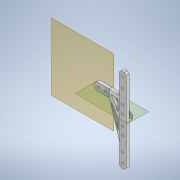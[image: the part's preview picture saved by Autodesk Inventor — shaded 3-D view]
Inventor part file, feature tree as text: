
AUTODESK INVENTOR PART (.ipt)
format: ipt  version: 2023 (Build 270158000, 158)  size: 307,200 bytes
history: native  units: mm
features: other x8, projected_geometry x7, sketch x6, extrude x5, fillet x4, plane x3, reference x3, chamfer x2, loft x1
ambient origin geometry x8: Origin, YZ Plane, XZ Plane, XY Plane, X Axis, Y Axis, Z Axis, Center Point
bodies: Solid1 (feature_tree)
feature tree (39):
  extrude  "Extrusion1"  Depth=87.0mm
  plane  "Work Plane1"
  plane  "Work Plane2"
  extrude  "Extrusion2"  Depth=2.0mm
  sketch  "Sketch3"  dims[d4=2.0mm d5=2.0mm]
  loft  "Loft1"
  plane  "Work Plane3"
  extrude  "Extrusion3"  Depth=8.0mm
  fillet  "Fillet1"  Radius=15.0mm
  extrude  "Extrusion4"  Depth=2.0mm
  fillet  "Fillet2"  Radius=3.0mm
  fillet  "Fillet3"  Radius=3.0mm
  chamfer  "Chamfer1"  Distance=3.0mm
  chamfer  "Chamfer2"  Distance=20.0mm
  extrude  "Extrusion5"  TaperAngle=0.0deg  [1 undecoded]
  fillet  "Fillet4"  [1 undecoded]
  sketch  "Sketch1"  dims[d0=7.0mm d1=87.0mm]
  reference  "Reference1"
  reference  "Reference2"
  sketch  "Sketch2"  dims[d2=2.0mm d3=2.0mm]
  reference  "Reference3"
  projected_geometry  "Projected Loop1"
  other  "Edges1"
  sketch  "Sketch5"  dims[d6=3.0mm d7=0.0mm d8=8.0mm d9=15.0mm]
  projected_geometry  "Projected Loop3"
  projected_geometry  "Projected Loop4"
  sketch  "Sketch6"  dims[d10=2.0mm d11=2.0mm d12=3.0mm d13=0.0mm d14=3.0mm]
  projected_geometry  "Projected Loop5"
  projected_geometry  "Projected Loop6"
  sketch  "Sketch7"  dims[d15=20.0mm d16=3.0mm d17=20.0mm d18=0.0mm d19=90.0deg d20=0.0mm d21=90.0deg d22=5.0mm d23=2.0mm d24=0.0mm d25=3.0mm d26=2.0mm d27=2.0mm d28=4.0mm d29=4.0mm d30=2.0mm d31=2.0mm d32=3.0mm d33=0.0mm d34=0.5mm d35=1.0mm d36=1.5mm d37=3.0mm d38=2.0mm d39=2.0mm d40=45.0deg d41=2.0mm d42=2.0mm d43=45.0deg d44=15.0mm d45=8.0mm d46=15.0mm d47=8.0mm d48=2.0mm d49=2.0mm d50=2.0mm d51=2.0mm d52=3.0mm d53=0.0mm d54=1.0mm]
  projected_geometry  "Projected Loop7"
  projected_geometry  "Projected Loop8"
  parser-record x1  (decoder bookkeeping rows leaked as tree rows — omitted from the tree; the rows remain in map.json)
  other  "body_8d_1.iam"
  other  "leg_2d_1:2"
  other  "leg_holder_2:1"
  other  "leg_1_2d_MIR:2"
  other  "leg_holder_2_MIR:1"
  other  "body_linker_1_8d:1"
note: 2 required parameter values undecoded (feature->parameter linkage not recoverable at this tier; creation-order binding heuristic only, values carry confidence <= 0.55)
note: 1 file-system path scrubbed to <path> (originals preserved in map.json)
